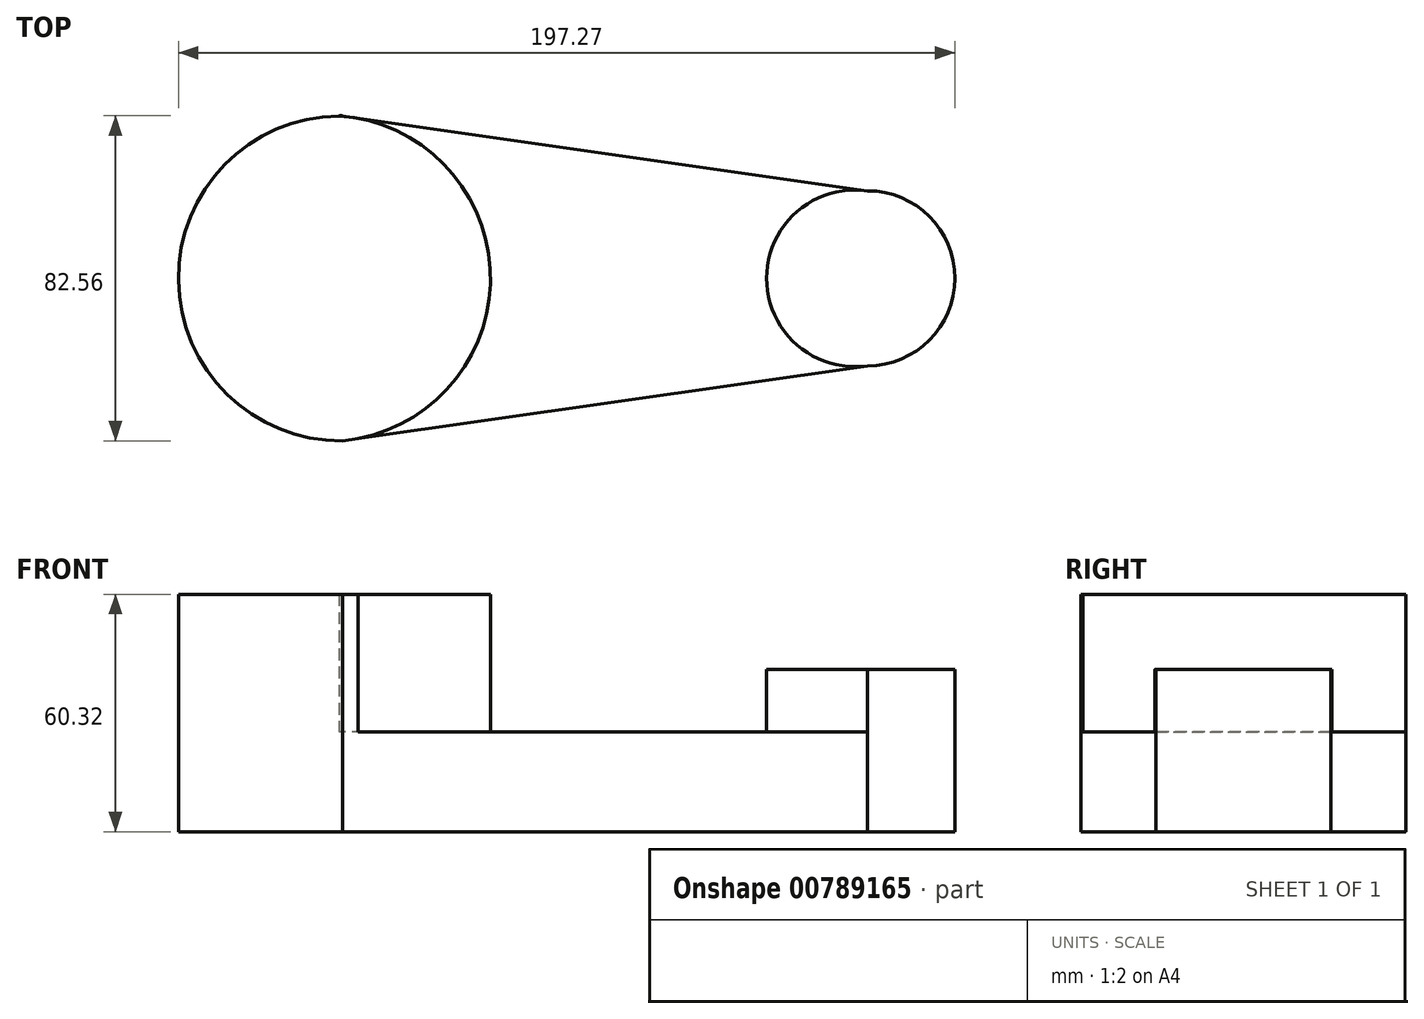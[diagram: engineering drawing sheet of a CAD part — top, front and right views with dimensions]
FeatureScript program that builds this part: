
annotation { "Feature Type Name" : "Feature", "Feature Type Description" : "" }
export const myFeature = defineFeature(function(context is Context, id is Id, definition is map)
    precondition{}
    {
        {
            var Q0;
            Q0=qCreatedBy(makeId("Top.planeOp"),FACE);
            var sketch = newSketch(context, id + "F0", { "sketchPlane" : qUnion([Q0])});
            skLineSegment(sketch, "E0", {"start": v(0, 0) * mm, "end": v(133.35, 0) * mm, "construction": true});
            skLineSegment(sketch, "E1", {"start": v(0, 0) * mm, "end": v(0, 41.28) * mm, "construction": true});
            skLineSegment(sketch, "E2", {"start": v(0, 0) * mm, "end": v(0, -41.28) * mm, "construction": true});
            skArc(sketch, "E3", {"start": v(0, 41.28) * mm, "mid": v(-41.73, 0) * mm, "end": v(0, -41.28) * mm, "construction": true});
            skArc(sketch, "E4", {"start": v(0, 41.28) * mm, "mid": v(-41.7, 0) * mm, "end": v(0, -41.28) * mm});
            skLineSegment(sketch, "E5", {"start": v(133.35, 0) * mm, "end": v(133.35, 22.23) * mm, "construction": true});
            skLineSegment(sketch, "E6", {"start": v(133.35, 0) * mm, "end": v(133.35, -22.23) * mm, "construction": true});
            skArc(sketch, "E7", {"start": v(133.35, -22.23) * mm, "mid": v(155.58, 0) * mm, "end": v(133.35, 22.23) * mm});
            skLineSegment(sketch, "E8", {"start": v(0, 41.27) * mm, "end": v(133.35, 22.23) * mm});
            skLineSegment(sketch, "E9", {"start": v(0, -41.27) * mm, "end": v(133.35, -22.23) * mm});
            skSolve(sketch);
        }
        {
            var Q0;
            Q0=makeQuery(id+"F0.imprint","IMPRINT",FACE,{"disambiguationData":[TD([[makeQuery(id+"F0.imprint","IMPRINT",EDGE,{"derivedFrom":sQuery(id+"F0.wireOp",EDGE,"E4")}),1.0]])]});
            var sketch = newSketch(context, id + "F1", { "sketchPlane" : qUnion([Q0])});
            skSolve(sketch);
        }
        {
            var Q0;
            Q0 = qSketchRegion(id + "F1", true);
            var Q1;
            Q1=makeQuery(id+"F0.imprint","IMPRINT",FACE,{"disambiguationData":[TD([[makeQuery(id+"F0.imprint","IMPRINT",EDGE,{"derivedFrom":sQuery(id+"F0.wireOp",EDGE,"E4")}),1.0]])]});
            extrude(context, id + "F2", {"entities" : qUnion([Q0, Q1]), "depth" : 25.4 * mm, "offsetDistance" : 25.4 * mm});
        }
        {
            var Q0;
            Q0=makeQuery(id+"F2.opExtrude","CAP_FACE",FACE,{"disambiguationData":[OSD([sQuery(id+"F0.wireOp",EDGE,"E4"),sQuery(id+"F0.wireOp",EDGE,"E7"),sQuery(id+"F0.wireOp",EDGE,"E8"),sQuery(id+"F0.wireOp",EDGE,"E9")])],"isStart":false});
            var sketch = newSketch(context, id + "F3", { "sketchPlane" : qUnion([Q0])});
            skArc(sketch, "E10", {"start": v(0, -41.28) * mm, "mid": v(37.56, 0.4) * mm, "end": v(-0.85, 41.28) * mm});
            skArc(sketch, "E11", {"start": v(133.35, 22.22) * mm, "mid": v(107.72, 0) * mm, "end": v(133.35, -22.22) * mm});
            skSolve(sketch);
        }
        {
            var Q0;
            Q0 = qSketchRegion(id + "F3", true);
            var Q1;
            {var subQ0=sQuery(id+"F3.wireOp",EDGE,"E10");var subQ1=makeQuery(id+"F2.opExtrude","CAP_EDGE",EDGE,{"disambiguationData":[OSD([sQuery(id+"F0.wireOp",EDGE,"E4")])],"isStart":false});var subQ2=makeQuery(id+"F3.imprint","INTERSECT",VERTEX,{"derivedFrom":[subQ1,subQ0]});Q1=makeQuery(id+"F3.imprint","IMPRINT",FACE,{"disambiguationData":[TD([[makeQuery(id+"F3.imprint","IMPRINT",EDGE,{"disambiguationData":[TD([[subQ2,1.0]])],"derivedFrom":subQ0}),1.0]])]});}
            extrude(context, id + "F4", {"entities" : qUnion([Q0, Q1]), "operationType" : NewBodyOperationType.ADD, "depth" : 34.92 * mm, "offsetDistance" : 25.4 * mm});
        }
        {
            var Q0;
            Q0=makeQuery(id+"F2.opExtrude","CAP_FACE",FACE,{"disambiguationData":[OSD([sQuery(id+"F0.wireOp",EDGE,"E4"),sQuery(id+"F0.wireOp",EDGE,"E7"),sQuery(id+"F0.wireOp",EDGE,"E8"),sQuery(id+"F0.wireOp",EDGE,"E9")])],"isStart":false});
            var sketch = newSketch(context, id + "F5", { "sketchPlane" : qUnion([Q0])});
            skArc(sketch, "E12", {"start": v(133.35, 22.22) * mm, "mid": v(107.72, 0) * mm, "end": v(133.35, -22.22) * mm});
            skSolve(sketch);
        }
        {
            var Q0;
            Q0 = qSketchRegion(id + "F5", true);
            var Q1;
            Q1=makeQuery(id+"F5.imprint","IMPRINT",FACE,{"disambiguationData":[TD([[makeQuery(id+"F5.imprint","IMPRINT",EDGE,{"derivedFrom":sQuery(id+"F5.wireOp",EDGE,"E12")}),1.0]])]});
            extrude(context, id + "F6", {"entities" : qUnion([Q0, Q1]), "operationType" : NewBodyOperationType.ADD, "depth" : 15.88 * mm, "offsetDistance" : 25.4 * mm});
        }
    });
